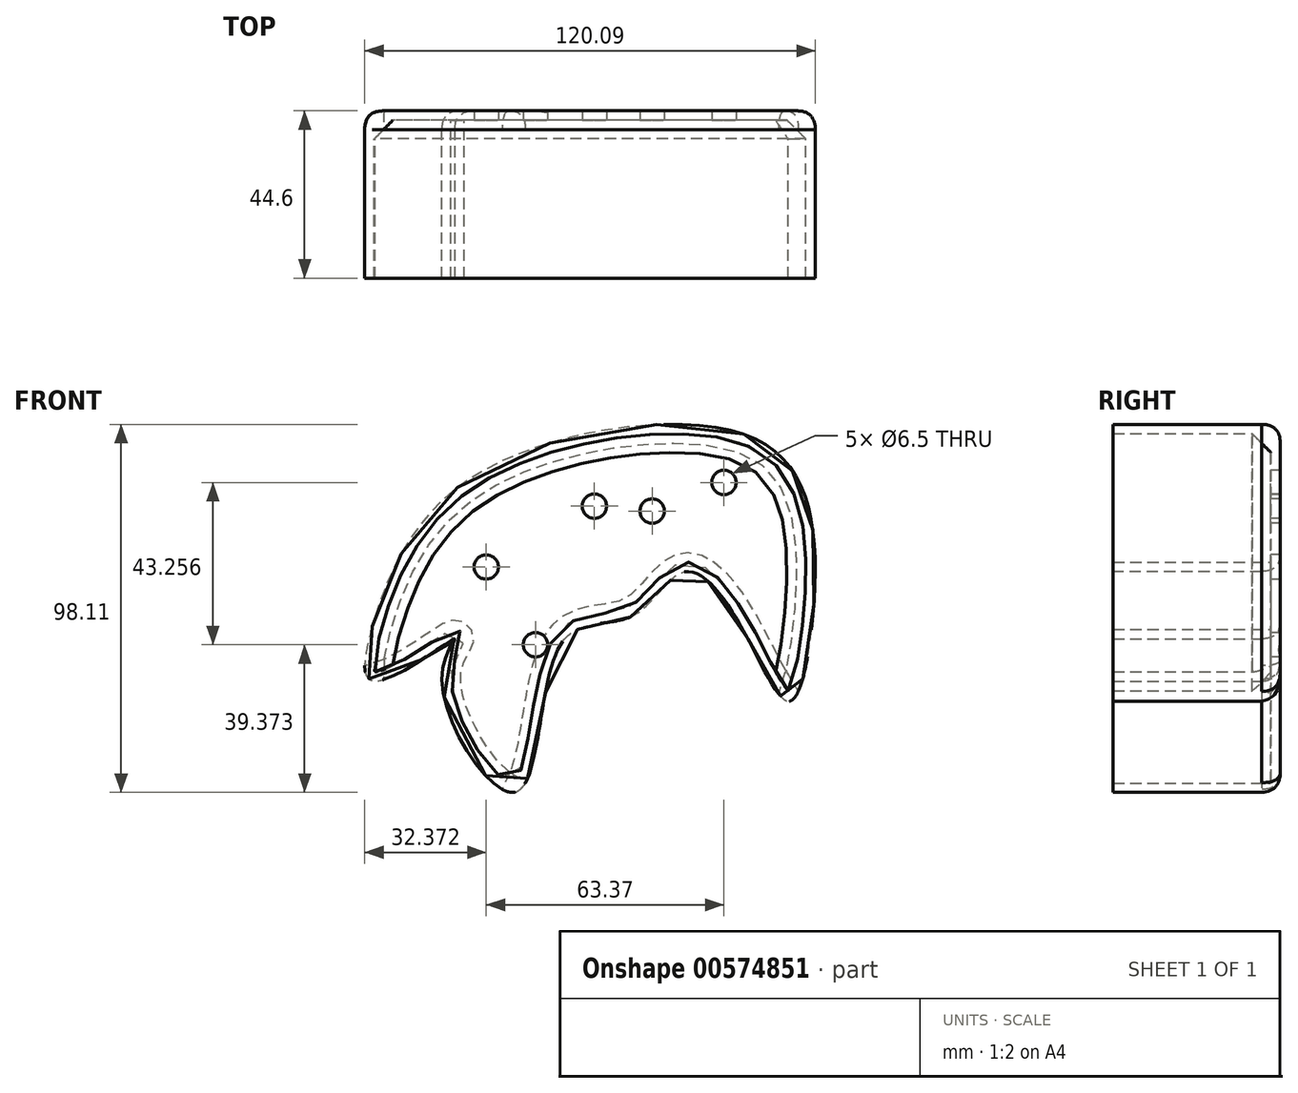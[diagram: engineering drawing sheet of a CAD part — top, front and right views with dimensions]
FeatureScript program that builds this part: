
annotation { "Feature Type Name" : "Feature", "Feature Type Description" : "" }
export const myFeature = defineFeature(function(context is Context, id is Id, definition is map)
    precondition{}
    {
        {
            var Q0;
            Q0=qCreatedBy(makeId("Front.planeOp"),FACE);
            var sketch = newSketch(context, id + "F0", { "sketchPlane" : qUnion([Q0])});
            skFitSpline(sketch, "E0", {"points": [v(-66.67, -15.88) * mm, v(-41.23, 23.14) * mm, v(27.49, 36.73) * mm, v(47.87, 20.93) * mm, v(50.7, -13.66) * mm, v(44.4, -35.78) * mm, v(31.12, -14.93) * mm, v(16.27, -1.34) * mm, v(2.69, -13.03) * mm, v(-16.11, -20.14) * mm, v(-28.44, -59.95) * mm, v(-48.18, -29.15) * mm, v(-44.86, -19.2) * mm, v(-66.03, -30.4) * mm, v(-66.67, -15.88) * mm]});
            skSolve(sketch);
        }
        {
            var Q0;
            Q0=makeQuery(id+"F0.imprint","IMPRINT",FACE,{"disambiguationData":[TD([[makeQuery(id+"F0.imprint","IMPRINT",EDGE,{"derivedFrom":sQuery(id+"F0.wireOp",EDGE,"E0")}),-1.0]])]});
            extrude(context, id + "F1", {"entities" : qUnion([Q0]), "depth" : 44.6 * mm, "offsetDistance" : 25 * mm});
        }
        {
            var Q0;
            Q0=makeQuery(id+"F1.opExtrude","CAP_FACE",FACE,{"disambiguationData":[OSD([sQuery(id+"F0.wireOp",EDGE,"E0")])],"isStart":false});
            shell(context, id + "F2", {"entities" : qUnion([Q0]), "thickness" : 2.5 * mm});
        }
        {
            var Q0;
            Q0=makeQuery(id+"F1.opExtrude","CAP_EDGE",EDGE,{"disambiguationData":[OSD([sQuery(id+"F0.wireOp",EDGE,"E0")])],"isStart":true});
            fillet(context, id + "F3", {"entities" : qUnion([Q0]), "radius" : 5 * mm, "tangentPropagation" : true, "rho" : 0.5, "crossSection" : FilletCrossSection.CONIC, "allowEdgeOverflow" : false});
        }
        {
            var Q0;
            {var subQ0=sQuery(id+"F0.wireOp",EDGE,"E0");Q0=makeQuery(id+"F2.opShell","OFFSET_EDGE",EDGE,{"disambiguationData":[OSD([subQ0]),TDD([makeQuery(id+"F1.opExtrude","CAP_EDGE",EDGE,{"disambiguationData":[OSD([subQ0])],"isStart":true})]),OD(1.0)]});}
            chamfer(context, id + "F4", {"entities" : qUnion([Q0]), "width" : 5 * mm, "tangentPropagation" : true});
        }
        {
            var Q0;
            {var subQ0=sQuery(id+"F0.wireOp",EDGE,"E0");Q0=makeQuery(id+"F2.opShell","OFFSET_FACE",FACE,{"disambiguationData":[OSD([subQ0]),TDD([makeQuery(id+"F1.opExtrude","CAP_FACE",FACE,{"disambiguationData":[OSD([subQ0])],"isStart":true})])]});}
            var sketch = newSketch(context, id + "F5", { "sketchPlane" : qUnion([Q0])});
            skPoint(sketch, "E1", {"position": v(27.05, 22.54) * mm});
            skPoint(sketch, "E2", {"position": v(-7.47, 16.23) * mm});
            skPoint(sketch, "E3", {"position": v(-36.32, 0) * mm});
            skPoint(sketch, "E4", {"position": v(-23.18, -20.72) * mm});
            skPoint(sketch, "E5", {"position": v(7.93, 14.9) * mm});
            skSolve(sketch);
        }
        {
            var Q0;
            Q0=sQuery(id+"F5.wireOp",VERTEX,"E2");
            var Q1;
            Q1=sQuery(id+"F5.wireOp",VERTEX,"E3");
            var Q2;
            Q2=sQuery(id+"F5.wireOp",VERTEX,"E4");
            var Q3;
            Q3=sQuery(id+"F5.wireOp",VERTEX,"E5");
            var Q4;
            Q4=sQuery(id+"F5.wireOp",VERTEX,"E1");
            var Q5;
            Q5=makeQuery(id+"F1.opExtrude","SWEPT_BODY",BODY,{"disambiguationData":[OSD([sQuery(id+"F0.wireOp",EDGE,"E0")])]});
            hole(context, id + "F6", {"style" : HoleStyle.C_BORE, "endStyle" : HoleEndStyle.THROUGH, "standardTappedOrClearance" : lookupTablePath({ "standard" : "ISO", "engagement" : "75%", "pitch" : "0.5 mm", "size" : "M3", "type" : "Tapped" }), "standardBlindInLast" : lookupTablePath({ "standard" : "ISO", "engagement" : "75%", "pitch" : "0.5 mm", "size" : "M3", "type" : "Tapped" }), "holeDiameter" : 2.5 * mm, "cBoreDiameter" : 6.5 * mm, "cBoreDepth" : 3 * mm, "showTappedDepth" : true, "isTappedThrough" : true, "tappedDepth" : 12 * mm, "tapClearance" : 3, "locations" : qUnion([Q0, Q1, Q2, Q3, Q4]), "scope" : qUnion([Q5]), "majorDiameter" : 3 * mm});
        }
    });
